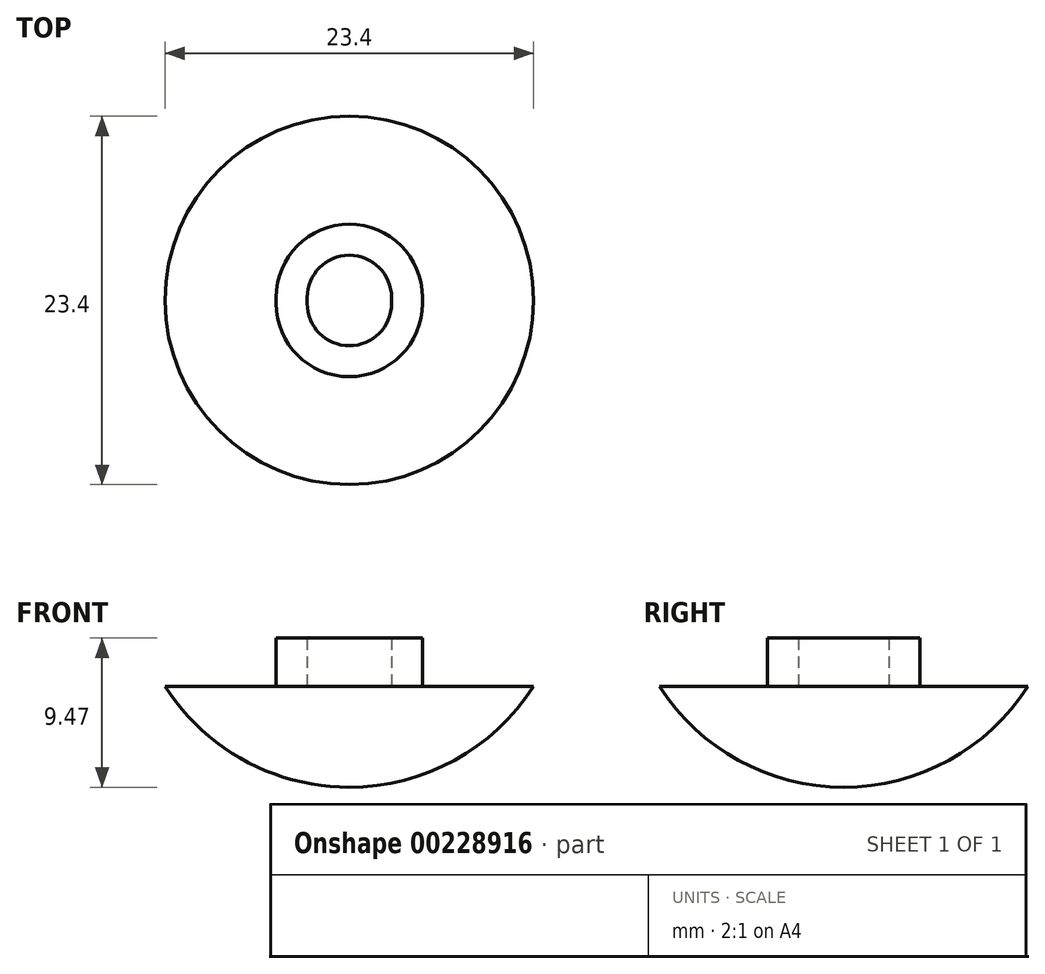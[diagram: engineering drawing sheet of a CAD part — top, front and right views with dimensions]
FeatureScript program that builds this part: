
annotation { "Feature Type Name" : "Feature", "Feature Type Description" : "" }
export const myFeature = defineFeature(function(context is Context, id is Id, definition is map)
    precondition{}
    {
        {
            var Q0;
            Q0=qCreatedBy(makeId("Front.planeOp"),FACE);
            var sketch = newSketch(context, id + "F0", { "sketchPlane" : qUnion([Q0])});
            skLineSegment(sketch, "E0", {"start": v(0, 0) * mm, "end": v(0, 6.4) * mm});
            skLineSegment(sketch, "E1", {"start": v(0, 6.4) * mm, "end": v(11.7, 6.4) * mm});
            skArc(sketch, "E2", {"start": v(0, 0) * mm, "mid": v(6.67, 1.7) * mm, "end": v(11.7, 6.4) * mm});
            skPoint(sketch, "E3.MirrorCS.end.orphan", {"position": v(-11.7, 6.4) * mm});
            skPoint(sketch, "E3.MirrorCS.start.orphan", {"position": v(0, 6.4) * mm});
            skPoint(sketch, "E4", {"position": v(11.7, 6.4) * mm});
            skSolve(sketch);
        }
        {
            var Q0;
            Q0=makeQuery(id+"F0.imprint","IMPRINT",FACE,{"disambiguationData":[TD([[makeQuery(id+"F0.imprint","IMPRINT",EDGE,{"derivedFrom":sQuery(id+"F0.wireOp",EDGE,"E0")}),-1.0]])]});
            var Q1;
            Q1=sQuery(id+"F0.wireOp",EDGE,"E0");
            revolve(context, id + "F1", {"entities" : qUnion([Q0]), "axis" : qUnion([Q1]), "revolveType" : RevolveType.FULL});
        }
        {
            var Q0;
            Q0=makeQuery(id+"F1.opRevolve","SWEPT_FACE",FACE,{"disambiguationData":[OSD([sQuery(id+"F0.wireOp",EDGE,"E1")])]});
            var sketch = newSketch(context, id + "F2", { "sketchPlane" : qUnion([Q0])});
            skLineSegment(sketch, "E5.left", {"start": v(4.65, 0.19) * mm, "end": v(4.65, -0.2) * mm});
            skLineSegment(sketch, "E5.right", {"start": v(-4.65, 0.19) * mm, "end": v(-4.65, -0.2) * mm});
            skPoint(sketch, "E5.middle", {"position": v(0, 0) * mm});
            skArc(sketch, "E6", {"start": v(-4.65, 0.19) * mm, "mid": v(0, 4.84) * mm, "end": v(4.65, 0.19) * mm});
            skArc(sketch, "E7", {"start": v(-4.65, -0.2) * mm, "mid": v(0, -4.84) * mm, "end": v(4.65, -0.2) * mm});
            skArc(sketch, "E8.0", {"start": v(-2.68, 0.19) * mm, "mid": v(0, 2.87) * mm, "end": v(2.68, 0.19) * mm});
            skLineSegment(sketch, "E8.1", {"start": v(-2.68, 0.19) * mm, "end": v(-2.68, -0.2) * mm});
            skArc(sketch, "E8.2", {"start": v(-2.68, -0.2) * mm, "mid": v(0, -2.87) * mm, "end": v(2.68, -0.2) * mm});
            skLineSegment(sketch, "E8.3", {"start": v(2.68, 0.19) * mm, "end": v(2.68, -0.2) * mm});
            skSolve(sketch);
        }
        {
            var Q0;
            Q0 = qSketchRegion(id + "F2", true);
            extrude(context, id + "F3", {"entities" : qUnion([Q0]), "operationType" : NewBodyOperationType.ADD, "depth" : 5.82 * mm});
        }
        {
            var Q0;
            Q0=makeQuery(id+"F3.opExtrude","CAP_FACE",FACE,{"disambiguationData":[OSD([sQuery(id+"F2.wireOp",EDGE,"E5.left"),sQuery(id+"F2.wireOp",EDGE,"E5.right"),sQuery(id+"F2.wireOp",EDGE,"E6"),sQuery(id+"F2.wireOp",EDGE,"E7"),sQuery(id+"F2.wireOp",EDGE,"E8.0"),sQuery(id+"F2.wireOp",EDGE,"E8.1"),sQuery(id+"F2.wireOp",EDGE,"E8.2"),sQuery(id+"F2.wireOp",EDGE,"E8.3")])],"isStart":false});
            var sketch = newSketch(context, id + "F4", { "sketchPlane" : qUnion([Q0])});
            skArc(sketch, "E9.0", {"start": v(-2.68, 0.19) * mm, "mid": v(0, 2.87) * mm, "end": v(2.68, 0.19) * mm});
            skLineSegment(sketch, "E9.1", {"start": v(-2.68, 0.19) * mm, "end": v(-2.68, -0.2) * mm});
            skArc(sketch, "E9.2", {"start": v(-2.68, -0.2) * mm, "mid": v(0, -2.87) * mm, "end": v(2.68, -0.2) * mm});
            skLineSegment(sketch, "E9.3", {"start": v(2.68, 0.19) * mm, "end": v(2.68, -0.2) * mm});
            skSolve(sketch);
        }
        {
            var Q0;
            Q0=makeQuery(id+"F4.imprint","IMPRINT",FACE,{"disambiguationData":[TD([[makeQuery(id+"F4.imprint","IMPRINT",EDGE,{"derivedFrom":sQuery(id+"F4.wireOp",EDGE,"E9.0")}),-1.0]])]});
            extrude(context, id + "F5", {"entities" : qUnion([Q0]), "operationType" : NewBodyOperationType.REMOVE, "oppositeDirection" : true, "depth" : 7.75 * mm});
        }
        {
            var Q0;
            Q0=makeQuery(id+"F5.boolean.opBoolean","COPY",FACE,{"derivedFrom":makeQuery(id+"F5.opExtrude","CAP_FACE",FACE,{"disambiguationData":[OSD([sQuery(id+"F4.wireOp",EDGE,"E9.0"),sQuery(id+"F4.wireOp",EDGE,"E9.1"),sQuery(id+"F4.wireOp",EDGE,"E9.2"),sQuery(id+"F4.wireOp",EDGE,"E9.3")])],"isStart":false})});
            extrude(context, id + "F6", {"entities" : qUnion([Q0]), "operationType" : NewBodyOperationType.ADD, "depth" : 5 * mm, "offsetDistance" : 25 * mm});
        }
    });
